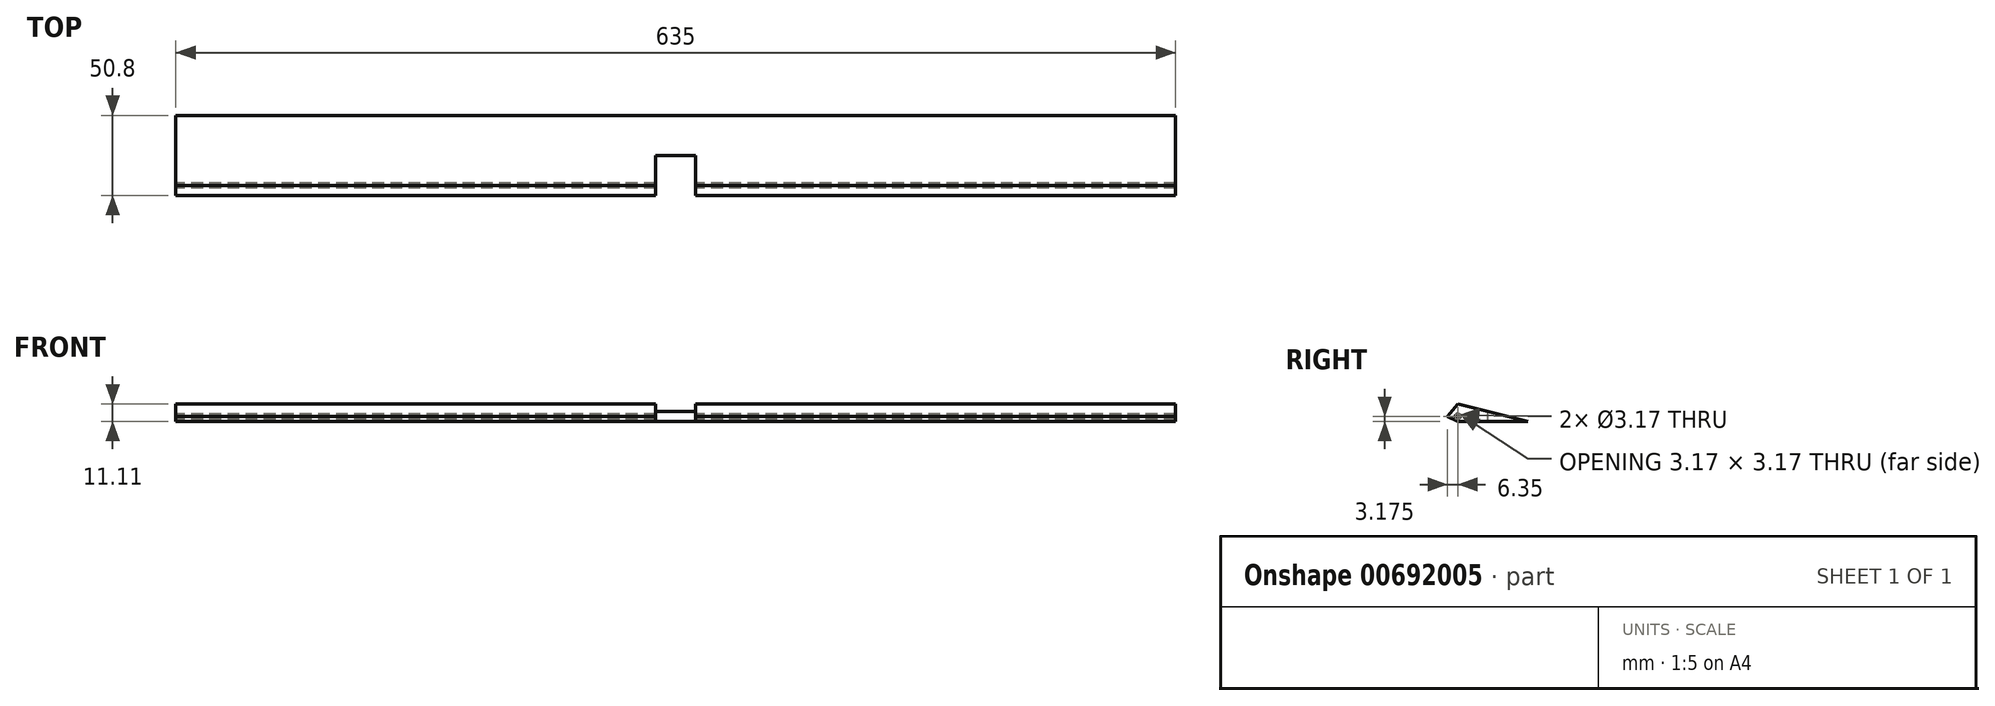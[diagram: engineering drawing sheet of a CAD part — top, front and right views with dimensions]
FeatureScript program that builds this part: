
annotation { "Feature Type Name" : "Feature", "Feature Type Description" : "" }
export const myFeature = defineFeature(function(context is Context, id is Id, definition is map)
    precondition{}
    {
        {
            var Q0;
            Q0=qCreatedBy(makeId("Right.planeOp"),FACE);
            var sketch = newSketch(context, id + "F0", { "sketchPlane" : qUnion([Q0])});
            skLineSegment(sketch, "E0.bottom", {"start": v(-127, 19.05) * mm, "end": v(127, 19.05) * mm});
            skLineSegment(sketch, "E0.top", {"start": v(-127, -19.05) * mm, "end": v(127, -19.05) * mm});
            skLineSegment(sketch, "E0.left", {"start": v(-127, 19.05) * mm, "end": v(-127, -19.05) * mm});
            skLineSegment(sketch, "E0.right", {"start": v(127, 19.05) * mm, "end": v(127, -19.05) * mm});
            skPoint(sketch, "E0.middle", {"position": v(0, 0) * mm});
            skLineSegment(sketch, "E1", {"start": v(-127, -19.05) * mm, "end": v(-127, -15.88) * mm});
            skLineSegment(sketch, "E2", {"start": v(-127, -19.05) * mm, "end": v(-120.65, -19.05) * mm});
            skLineSegment(sketch, "E3", {"start": v(-120.65, -19.05) * mm, "end": v(-127, -15.88) * mm});
            skLineSegment(sketch, "E4", {"start": v(-127, 19.05) * mm, "end": v(-76.2, 19.05) * mm});
            skLineSegment(sketch, "E5", {"start": v(-76.2, 19.05) * mm, "end": v(-76.2, 6.35) * mm});
            skLineSegment(sketch, "E6", {"start": v(-127, 19.05) * mm, "end": v(-25.4, 19.05) * mm});
            skLineSegment(sketch, "E7", {"start": v(-25.4, 19.05) * mm, "end": v(-76.2, 6.35) * mm});
            skLineSegment(sketch, "E8", {"start": v(-76.2, 6.35) * mm, "end": v(-127, -15.88) * mm});
            skLineSegment(sketch, "E9", {"start": v(-25.4, 19.05) * mm, "end": v(127, -19.05) * mm});
            skSolve(sketch);
        }
        {
            var Q0;
            {var subQ0=sQuery(id+"F0.wireOp",EDGE,"E3");Q0=makeQuery(id+"F0.imprint","IMPRINT",FACE,{"disambiguationData":[TD([[makeQuery(id+"F0.imprint","IMPRINT",EDGE,{"derivedFrom":subQ0}),-1.0]])]});}
            extrude(context, id + "F1", {"entities" : qUnion([Q0]), "depth" : 762 * mm, "offsetDistance" : 25.4 * mm});
        }
        {
            var Q0;
            Q0=makeQuery(id+"F1.opExtrude","SWEPT_FACE",FACE,{"disambiguationData":[OSD([sQuery(id+"F0.wireOp",EDGE,"E0.top")])]});
            var sketch = newSketch(context, id + "F2", { "sketchPlane" : qUnion([Q0])});
            skLineSegment(sketch, "E10", {"start": v(0, -127) * mm, "end": v(76.2, -127) * mm});
            skLineSegment(sketch, "E11", {"start": v(76.2, -127) * mm, "end": v(76.2, -76.2) * mm});
            skLineSegment(sketch, "E12", {"start": v(76.2, -76.2) * mm, "end": v(711.2, -76.2) * mm});
            skLineSegment(sketch, "E13", {"start": v(711.2, -76.2) * mm, "end": v(711.2, -127) * mm});
            skLineSegment(sketch, "E14", {"start": v(76.2, -76.2) * mm, "end": v(393.7, -76.2) * mm});
            skLineSegment(sketch, "E15", {"start": v(393.7, -76.2) * mm, "end": v(393.7, -101.6) * mm});
            skLineSegment(sketch, "E16", {"start": v(393.7, -101.6) * mm, "end": v(406.4, -101.6) * mm});
            skLineSegment(sketch, "E17", {"start": v(406.4, -101.6) * mm, "end": v(381, -101.6) * mm});
            skLineSegment(sketch, "E18", {"start": v(381, -101.6) * mm, "end": v(381, -76.2) * mm});
            skLineSegment(sketch, "E19", {"start": v(406.4, -101.6) * mm, "end": v(406.4, -76.2) * mm});
            skSolve(sketch);
        }
        {
            var Q0;
            Q0=makeQuery(id+"F2.imprint","IMPRINT",FACE,{"disambiguationData":[TD([[makeQuery(id+"F2.imprint","IMPRINT",EDGE,{"derivedFrom":sQuery(id+"F2.wireOp",EDGE,"E10")}),-1.0]])]});
            var Q1;
            Q1=makeQuery(id+"F1.opExtrude","SWEPT_FACE",FACE,{"disambiguationData":[OSD([sQuery(id+"F0.wireOp",EDGE,"E3")])]});
            var Q2;
            {var subQ0=sQuery(id+"F2.wireOp",EDGE,"E15");Q2=makeQuery(id+"F2.imprint","IMPRINT",FACE,{"disambiguationData":[TD([[makeQuery(id+"F2.imprint","IMPRINT",EDGE,{"derivedFrom":subQ0}),-1.0]])]});}
            var Q3;
            {var subQ2=sQuery(id+"F2.wireOp",EDGE,"E15");Q3=makeQuery(id+"F2.imprint","IMPRINT",FACE,{"disambiguationData":[TD([[makeQuery(id+"F2.imprint","IMPRINT",EDGE,{"derivedFrom":subQ2}),1.0]])]});}
            extrude(context, id + "F3", {"entities" : qUnion([Q0, Q1, Q2, Q3]), "operationType" : NewBodyOperationType.REMOVE, "endBound" : BoundingType.THROUGH_ALL, "oppositeDirection" : true, "depth" : 25.4 * mm, "offsetDistance" : 25.4 * mm});
        }
        {
            var Q0;
            Q0=makeQuery(id+"F3.boolean.opBoolean","COPY",FACE,{"derivedFrom":makeQuery(id+"F3.opExtrude","SWEPT_FACE",FACE,{"disambiguationData":[OSD([sQuery(id+"F2.wireOp",EDGE,"E11")])]})});
            var sketch = newSketch(context, id + "F4", { "sketchPlane" : qUnion([Q0])});
            skLineSegment(sketch, "E20", {"start": v(-127, -19.05) * mm, "end": v(-82.55, -19.05) * mm});
            skLineSegment(sketch, "E21", {"start": v(-82.55, -19.05) * mm, "end": v(-82.55, -7.94) * mm});
            skLineSegment(sketch, "E22", {"start": v(-127, -19.05) * mm, "end": v(-88.9, -19.05) * mm});
            skLineSegment(sketch, "E23", {"start": v(-88.9, -19.05) * mm, "end": v(-88.9, -9.53) * mm});
            skLineSegment(sketch, "E24", {"start": v(-76.2, -19.05) * mm, "end": v(-76.2, -15.88) * mm});
            skLineSegment(sketch, "E25", {"start": v(-76.2, -15.88) * mm, "end": v(-82.55, -19.05) * mm});
            skLineSegment(sketch, "E26", {"start": v(-76.2, -15.88) * mm, "end": v(-82.55, -7.94) * mm});
            skSolve(sketch);
        }
        {
            var Q0;
            {var subQ0=sQuery(id+"F4.wireOp",EDGE,"RdxC5ClE-TM9d-Ymyk-f1eb-UAKcxgaN80Cf");Q0=makeQuery(id+"F4.imprint","IMPRINT",FACE,{"disambiguationData":[TD([[makeQuery(id+"F4.imprint","IMPRINT",EDGE,{"derivedFrom":subQ0}),-1.0]])]});}
            var Q1;
            {var subQ0=sQuery(id+"F4.wireOp",EDGE,"HFo8b9Q3-XqX0-Gt14-9DyS-8aIeYXehCl1V");Q1=makeQuery(id+"F4.imprint","IMPRINT",FACE,{"disambiguationData":[TD([[makeQuery(id+"F4.imprint","IMPRINT",EDGE,{"derivedFrom":subQ0}),1.0]])]});}
            var Q2;
            {var subQ0=sQuery(id+"F4.wireOp",EDGE,"E26");Q2=makeQuery(id+"F4.imprint","IMPRINT",FACE,{"disambiguationData":[TD([[makeQuery(id+"F4.imprint","IMPRINT",EDGE,{"derivedFrom":subQ0}),-1.0]])]});}
            var Q3;
            {var subQ0=sQuery(id+"F4.wireOp",EDGE,"E24");Q3=makeQuery(id+"F4.imprint","IMPRINT",FACE,{"disambiguationData":[TD([[makeQuery(id+"F4.imprint","IMPRINT",EDGE,{"derivedFrom":subQ0}),-1.0]])]});}
            extrude(context, id + "F5", {"entities" : qUnion([Q0, Q1, Q2, Q3]), "operationType" : NewBodyOperationType.REMOVE, "endBound" : BoundingType.THROUGH_ALL, "oppositeDirection" : true, "depth" : 25.4 * mm, "offsetDistance" : 25.4 * mm});
        }
        {
            var Q0;
            Q0=makeQuery(id+"F3.boolean.opBoolean","COPY",FACE,{"derivedFrom":makeQuery(id+"F3.opExtrude","SWEPT_FACE",FACE,{"disambiguationData":[OSD([sQuery(id+"F2.wireOp",EDGE,"E11")])]})});
            var sketch = newSketch(context, id + "F6", { "sketchPlane" : qUnion([Q0])});
            skCircle(sketch, "E27", {"center": v(-82.55, -15.87) * mm, "radius": 1.59 * mm});
            skLineSegment(sketch, "E28", {"start": v(-82.55, -19.05) * mm, "end": v(-82.55, -17.46) * mm});
            skSolve(sketch);
        }
        {
            var Q0;
            Q0 = qSketchRegion(id + "F6", true);
            extrude(context, id + "F7", {"entities" : qUnion([Q0]), "operationType" : NewBodyOperationType.REMOVE, "endBound" : BoundingType.THROUGH_ALL, "oppositeDirection" : true, "depth" : 25.4 * mm, "offsetDistance" : 25.4 * mm});
        }
    });
